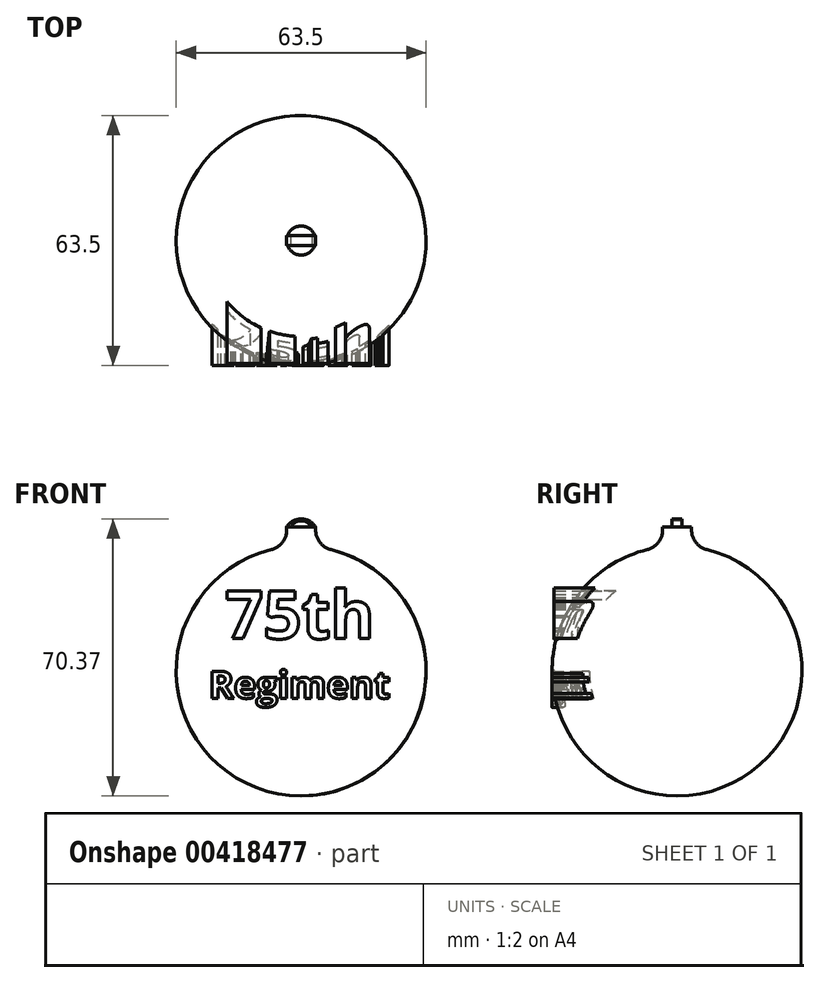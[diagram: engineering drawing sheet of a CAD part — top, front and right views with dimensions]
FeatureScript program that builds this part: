
annotation { "Feature Type Name" : "Feature", "Feature Type Description" : "" }
export const myFeature = defineFeature(function(context is Context, id is Id, definition is map)
    precondition{}
    {
        {
            var Q0;
            Q0=qCreatedBy(makeId("Front.planeOp"),FACE);
            var sketch = newSketch(context, id + "F0", { "sketchPlane" : qUnion([Q0])});
            skArc(sketch, "E0", {"start": v(0, 31.75) * mm, "mid": v(-31.75, 0) * mm, "end": v(0, -31.75) * mm});
            skLineSegment(sketch, "E1", {"start": v(0, 38.57) * mm, "end": v(0, -63.2) * mm});
            skSolve(sketch);
        }
        {
            var Q0;
            Q0=qSketchRegion(id+"F0",true);
            var Q1;
            Q1=sQuery(id+"F0.wireOp",EDGE,"E1");
            revolve(context, id + "F1", {"entities" : qUnion([Q0]), "axis" : qUnion([Q1]), "revolveType" : RevolveType.FULL});
        }
        {
            var Q0;
            Q0=qCreatedBy(makeId("Top.planeOp"),FACE);
            var sketch = newSketch(context, id + "F2", { "sketchPlane" : qUnion([Q0])});
            skCircle(sketch, "E2", {"center": v(0, 0) * mm, "radius": 3.69 * mm});
            skSolve(sketch);
        }
        {
            var Q0;
            Q0=qSketchRegion(id+"F2",true);
            extrude(context, id + "F3", {"entities" : qUnion([Q0]), "operationType" : NewBodyOperationType.ADD, "depth" : 36.58 * mm});
        }
        {
            var Q0;
            Q0=makeQuery(id+"F3.boolean.opBoolean","INTERSECT",EDGE,{"derivedFrom":[makeQuery(id+"F1.opRevolve","SWEPT_FACE",FACE,{"disambiguationData":[OSD([sQuery(id+"F0.wireOp",EDGE,"E0")])]}),makeQuery(id+"F3.opExtrude","SWEPT_FACE",FACE,{"disambiguationData":[OSD([sQuery(id+"F2.wireOp",EDGE,"E2")])]})]});
            fillet(context, id + "F4", {"entities" : qUnion([Q0]), "radius" : 5.08 * mm, "tangentPropagation" : true, "allowEdgeOverflow" : false});
        }
        {
            var Q0;
            Q0=qCreatedBy(makeId("Front.planeOp"),FACE);
            var sketch = newSketch(context, id + "F5", { "sketchPlane" : qUnion([Q0])});
            skLineSegment(sketch, "E3.0", {"start": v(-3.69, 36.58) * mm, "end": v(3.69, 36.58) * mm});
            skArc(sketch, "E4", {"start": v(3.69, 36.58) * mm, "mid": v(0, 38.62) * mm, "end": v(-3.69, 36.58) * mm});
            skSolve(sketch);
        }
        {
            var Q0;
            Q0=makeQuery(id+"F5.imprint","IMPRINT",FACE,{"disambiguationData":[TD([[makeQuery(id+"F5.imprint","IMPRINT",EDGE,{"derivedFrom":sQuery(id+"F5.wireOp",EDGE,"E3.0")}),1.0]])]});
            extrude(context, id + "F6", {"entities" : qUnion([Q0]), "operationType" : NewBodyOperationType.ADD, "endBound" : BoundingType.SYMMETRIC, "depth" : 2.54 * mm});
        }
        {
            var Q0;
            Q0=qCreatedBy(makeId("Front.planeOp"),FACE);
            var sketch = newSketch(context, id + "F7", { "sketchPlane" : qUnion([Q0])});
            skLineSegment(sketch, "E5.0", {"start": v(-3.46, 36.58) * mm, "end": v(3.46, 36.58) * mm});
            skArc(sketch, "E6", {"start": v(2.73, 36.58) * mm, "mid": v(0, 38.17) * mm, "end": v(-2.72, 36.58) * mm});
            skSolve(sketch);
        }
        {
            var Q0;
            Q0=qSketchRegion(id+"F7",true);
            extrude(context, id + "F8", {"entities" : qUnion([Q0]), "operationType" : NewBodyOperationType.REMOVE, "endBound" : BoundingType.SYMMETRIC, "oppositeDirection" : true, "depth" : 25.4 * mm});
        }
        {
            var Q0;
            Q0=qCreatedBy(makeId("Front.planeOp"),FACE);
            var sketch = newSketch(context, id + "F9", { "sketchPlane" : qUnion([Q0])});
            skText(sketch, "E7", { "text": "75th ", "fontName": "OpenSans-Bold.ttf"});
            const initialGuessF9  = {"E7": [-0.01929, 0.00821, 1, 0, 0.01222]};
            skSetInitialGuess(sketch, initialGuessF9);
            skSolve(sketch);
        }
        {
            var Q0;
            Q0=qSketchRegion(id+"F9",true);
            extrude(context, id + "F10", {"entities" : qUnion([Q0]), "operationType" : NewBodyOperationType.ADD, "depth" : 31.24 * mm});
        }
        {
            var Q0;
            Q0=qCreatedBy(makeId("Front.planeOp"),FACE);
            var sketch = newSketch(context, id + "F11", { "sketchPlane" : qUnion([Q0])});
            skText(sketch, "E8", { "text": "Regiment ", "fontName": "OpenSans-Bold.ttf"});
            const initialGuessF11  = {"E8": [-0.02346, -0.00694, 1, 0, 0.00694]};
            skSetInitialGuess(sketch, initialGuessF11);
            skSolve(sketch);
        }
        {
            var Q0;
            Q0=qSketchRegion(id+"F11",true);
            extrude(context, id + "F12", {"entities" : qUnion([Q0]), "operationType" : NewBodyOperationType.ADD, "depth" : 31.75 * mm});
        }
    });
